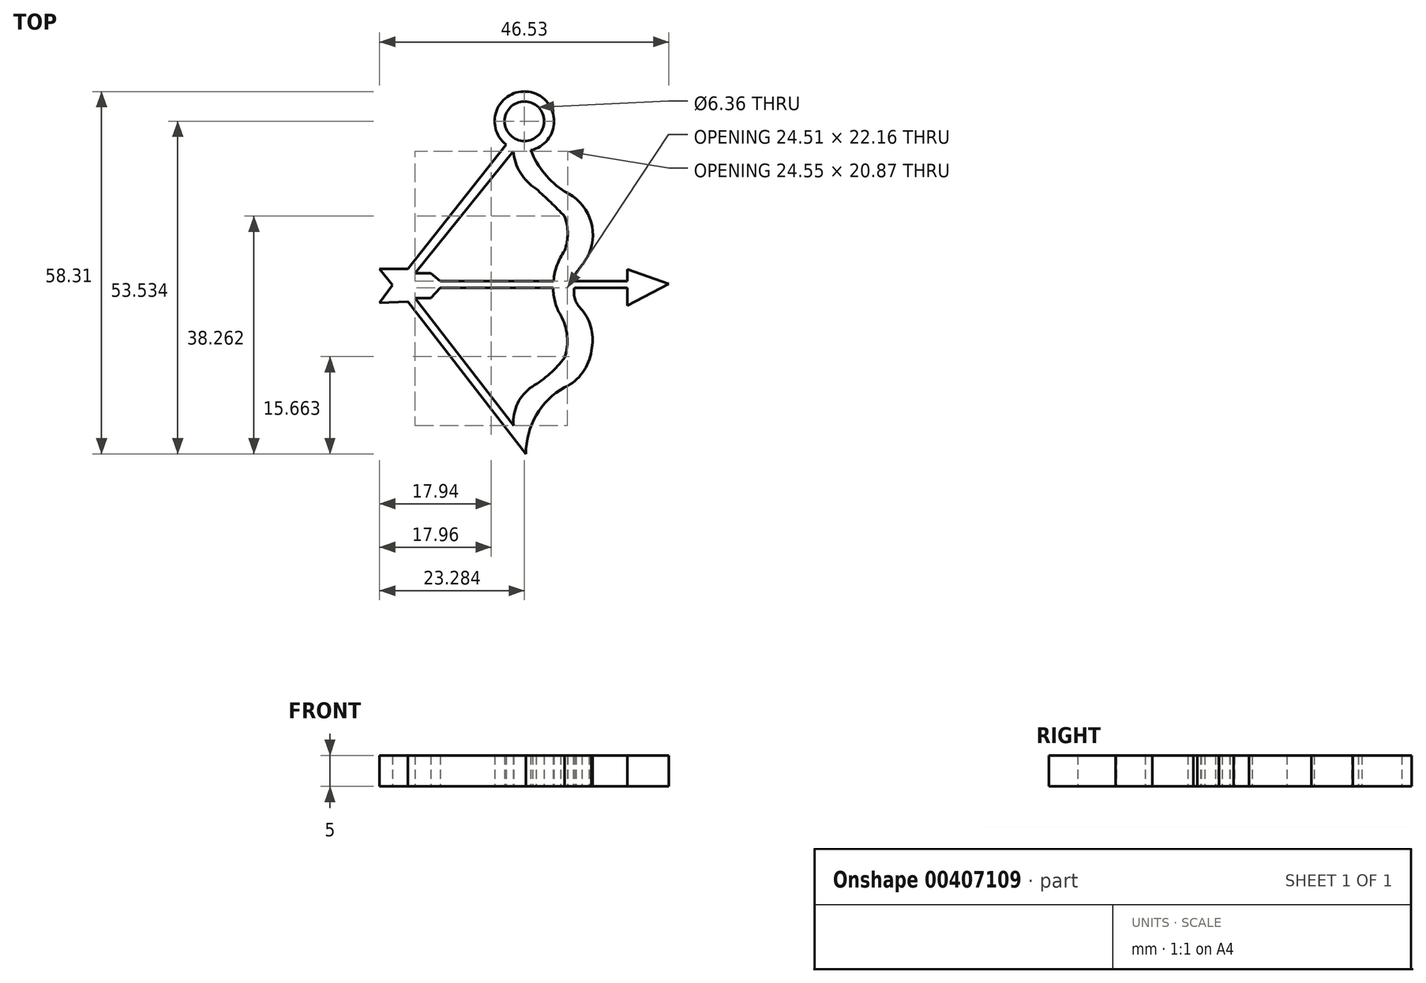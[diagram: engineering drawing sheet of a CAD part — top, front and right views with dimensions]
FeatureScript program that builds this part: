
annotation { "Feature Type Name" : "Feature", "Feature Type Description" : "" }
export const myFeature = defineFeature(function(context is Context, id is Id, definition is map)
    precondition{}
    {
        {
            var Q0;
            Q0=qCreatedBy(makeId("Top.planeOp"),FACE);
            var sketch = newSketch(context, id + "F0", { "sketchPlane" : qUnion([Q0])});
            skLineSegment(sketch, "E0", {"start": v(-8.25, 18.08) * mm, "end": v(-24.05, -1.55) * mm});
            skLineSegment(sketch, "E1", {"start": v(-24.05, -1.55) * mm, "end": v(-21.52, -1.55) * mm});
            skLineSegment(sketch, "E2", {"start": v(-21.52, -1.55) * mm, "end": v(-20, -2.78) * mm});
            skLineSegment(sketch, "E3", {"start": v(-20, -2.78) * mm, "end": v(10.1, -2.78) * mm});
            skLineSegment(sketch, "E4", {"start": v(10.1, -2.78) * mm, "end": v(10.1, -0.92) * mm});
            skLineSegment(sketch, "E5", {"start": v(10.1, -0.92) * mm, "end": v(16.8, -3.28) * mm});
            skLineSegment(sketch, "E6", {"start": v(16.8, -3.28) * mm, "end": v(10.1, -6.73) * mm});
            skLineSegment(sketch, "E7", {"start": v(10.1, -6.73) * mm, "end": v(10.1, -3.87) * mm});
            skLineSegment(sketch, "E8", {"start": v(10.1, -3.87) * mm, "end": v(-20, -3.87) * mm});
            skLineSegment(sketch, "E9", {"start": v(-20, -3.87) * mm, "end": v(-21.52, -5.56) * mm});
            skLineSegment(sketch, "E10", {"start": v(-21.52, -5.56) * mm, "end": v(-24.05, -5.56) * mm});
            skLineSegment(sketch, "E11", {"start": v(-24.05, -5.56) * mm, "end": v(-8.2, -26.03) * mm});
            skLineSegment(sketch, "E12", {"start": v(-6.22, -30.6) * mm, "end": v(-25.19, -6.13) * mm});
            skLineSegment(sketch, "E13", {"start": v(-25.19, -6.13) * mm, "end": v(-29.74, -6.28) * mm});
            skLineSegment(sketch, "E14", {"start": v(-29.74, -6.28) * mm, "end": v(-27.68, -3.47) * mm});
            skLineSegment(sketch, "E15", {"start": v(-27.68, -3.47) * mm, "end": v(-29.74, -0.8) * mm});
            skLineSegment(sketch, "E16", {"start": v(-29.74, -0.8) * mm, "end": v(-25.19, -0.8) * mm});
            skLineSegment(sketch, "E17", {"start": v(-25.19, -0.8) * mm, "end": v(-6.46, 22.92) * mm});
            skArc(sketch, "E18", {"start": v(-6.46, 22.92) * mm, "mid": v(-4.58, 16.49) * mm, "end": v(0, 11.59) * mm});
            skArc(sketch, "E19", {"start": v(3.96, 1.58) * mm, "mid": v(4.03, 7.4) * mm, "end": v(0, 11.59) * mm});
            skArc(sketch, "E20", {"start": v(1.85, -1.48) * mm, "mid": v(2.97, 0.01) * mm, "end": v(3.96, 1.58) * mm});
            skArc(sketch, "E21", {"start": v(1.85, -1.48) * mm, "mid": v(1.58, -2.1) * mm, "end": v(1.43, -2.78) * mm});
            skArc(sketch, "E22", {"start": v(0, -19.88) * mm, "mid": v(-4.56, -24.4) * mm, "end": v(-6.22, -30.6) * mm});
            skArc(sketch, "E23", {"start": v(0, -19.88) * mm, "mid": v(2.93, -17.5) * mm, "end": v(4.3, -13.98) * mm});
            skArc(sketch, "E24", {"start": v(4.3, -13.98) * mm, "mid": v(4.34, -10.53) * mm, "end": v(2.82, -7.43) * mm});
            skArc(sketch, "E25", {"start": v(1.57, -3.87) * mm, "mid": v(1.73, -5.81) * mm, "end": v(2.82, -7.43) * mm});
            skArc(sketch, "E26", {"start": v(-8.25, 18.08) * mm, "mid": v(-7.1, 14.64) * mm, "end": v(-4.57, 12.03) * mm});
            skArc(sketch, "E27", {"start": v(0, 7.62) * mm, "mid": v(-2.24, 9.88) * mm, "end": v(-4.57, 12.03) * mm});
            skArc(sketch, "E28", {"start": v(0, 2.09) * mm, "mid": v(0.5, 4.86) * mm, "end": v(0, 7.62) * mm});
            skArc(sketch, "E29", {"start": v(0, 2.09) * mm, "mid": v(-1.2, -0.24) * mm, "end": v(-1.77, -2.78) * mm});
            skArc(sketch, "E30", {"start": v(-1.83, -3.87) * mm, "mid": v(-1.53, -6.15) * mm, "end": v(-0.64, -8.28) * mm});
            skArc(sketch, "E31", {"start": v(0, -15.12) * mm, "mid": v(0.42, -11.63) * mm, "end": v(-0.64, -8.28) * mm});
            skArc(sketch, "E32", {"start": v(-5.17, -19.77) * mm, "mid": v(-2.36, -17.7) * mm, "end": v(0, -15.12) * mm});
            skArc(sketch, "E33", {"start": v(-5.17, -19.77) * mm, "mid": v(-7.55, -22.48) * mm, "end": v(-8.2, -26.03) * mm});
            skCircle(sketch, "E34", {"center": v(-6.46, 22.92) * mm, "radius": 3.18 * mm});
            skCircle(sketch, "E35.0", {"center": v(-6.46, 22.92) * mm, "radius": 4.78 * mm});
            skSolve(sketch);
        }
        {
            var Q0;
            Q0 = qSketchRegion(id + "F0", true);
            extrude(context, id + "F1", {"entities" : qUnion([Q0]), "depth" : 5 * mm});
        }
    });
